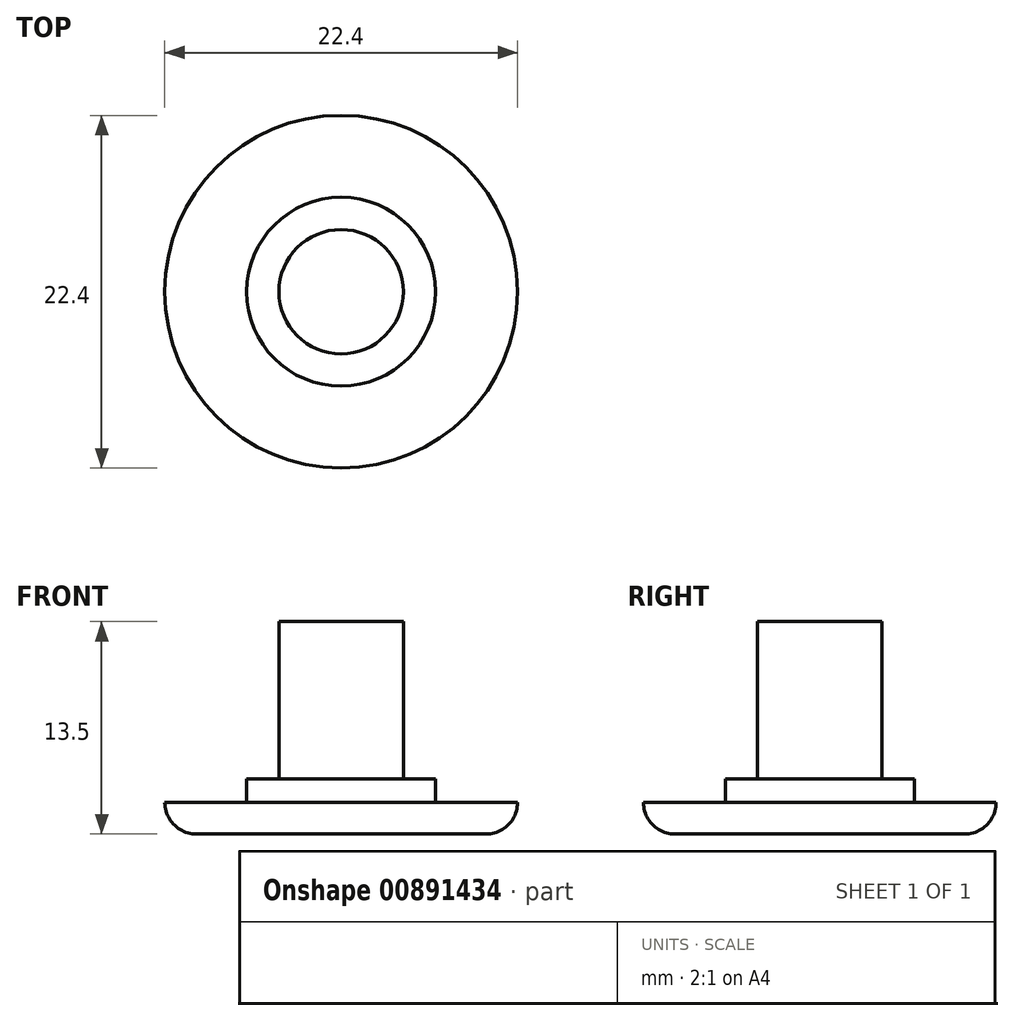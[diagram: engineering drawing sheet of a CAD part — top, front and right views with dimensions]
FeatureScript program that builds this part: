
annotation { "Feature Type Name" : "Feature", "Feature Type Description" : "" }
export const myFeature = defineFeature(function(context is Context, id is Id, definition is map)
    precondition{}
    {
        {
            var Q0;
            Q0=qCreatedBy(makeId("Top.planeOp"),FACE);
            var sketch = newSketch(context, id + "F0", { "sketchPlane" : qUnion([Q0])});
            skCircle(sketch, "E0", {"center": v(0, 0) * mm, "radius": 11.2 * mm});
            skSolve(sketch);
        }
        {
            var Q0;
            Q0=makeQuery(id+"F0.imprint","IMPRINT",FACE,{"disambiguationData":[TD([[makeQuery(id+"F0.imprint","IMPRINT",EDGE,{"derivedFrom":sQuery(id+"F0.wireOp",EDGE,"E0")}),1.0]])]});
            extrude(context, id + "F1", {"entities" : qUnion([Q0]), "depth" : 2 * mm, "offsetDistance" : 25 * mm});
        }
        {
            var Q0;
            Q0=makeQuery(id+"F1.opExtrude","CAP_FACE",FACE,{"disambiguationData":[OSD([sQuery(id+"F0.wireOp",EDGE,"E0")])],"isStart":false});
            var sketch = newSketch(context, id + "F2", { "sketchPlane" : qUnion([Q0])});
            skCircle(sketch, "E1", {"center": v(0, 0) * mm, "radius": 6 * mm});
            skSolve(sketch);
        }
        {
            var Q0;
            Q0=makeQuery(id+"F2.imprint","IMPRINT",FACE,{"disambiguationData":[TD([[makeQuery(id+"F2.imprint","IMPRINT",EDGE,{"derivedFrom":sQuery(id+"F2.wireOp",EDGE,"E1")}),1.0]])]});
            extrude(context, id + "F3", {"entities" : qUnion([Q0]), "operationType" : NewBodyOperationType.ADD, "depth" : 1.5 * mm, "offsetDistance" : 25 * mm});
        }
        {
            var Q0;
            Q0=makeQuery(id+"F3.opExtrude","CAP_FACE",FACE,{"disambiguationData":[OSD([sQuery(id+"F2.wireOp",EDGE,"E1")])],"isStart":false});
            var sketch = newSketch(context, id + "F4", { "sketchPlane" : qUnion([Q0])});
            skCircle(sketch, "E2", {"center": v(0, 0) * mm, "radius": 3.95 * mm});
            skSolve(sketch);
        }
        {
            var Q0;
            Q0=makeQuery(id+"F4.imprint","IMPRINT",FACE,{"disambiguationData":[TD([[makeQuery(id+"F4.imprint","IMPRINT",EDGE,{"derivedFrom":sQuery(id+"F4.wireOp",EDGE,"E2")}),1.0]])]});
            extrude(context, id + "F5", {"entities" : qUnion([Q0]), "operationType" : NewBodyOperationType.ADD, "depth" : 10 * mm, "offsetDistance" : 25 * mm});
        }
        {
            var Q0;
            Q0=makeQuery(id+"F1.opExtrude","CAP_FACE",FACE,{"disambiguationData":[OSD([sQuery(id+"F0.wireOp",EDGE,"E0")])],"isStart":true});
            fillet(context, id + "F6", {"entities" : qUnion([Q0]), "radius" : 2 * mm, "tangentPropagation" : true, "allowEdgeOverflow" : false});
        }
    });
